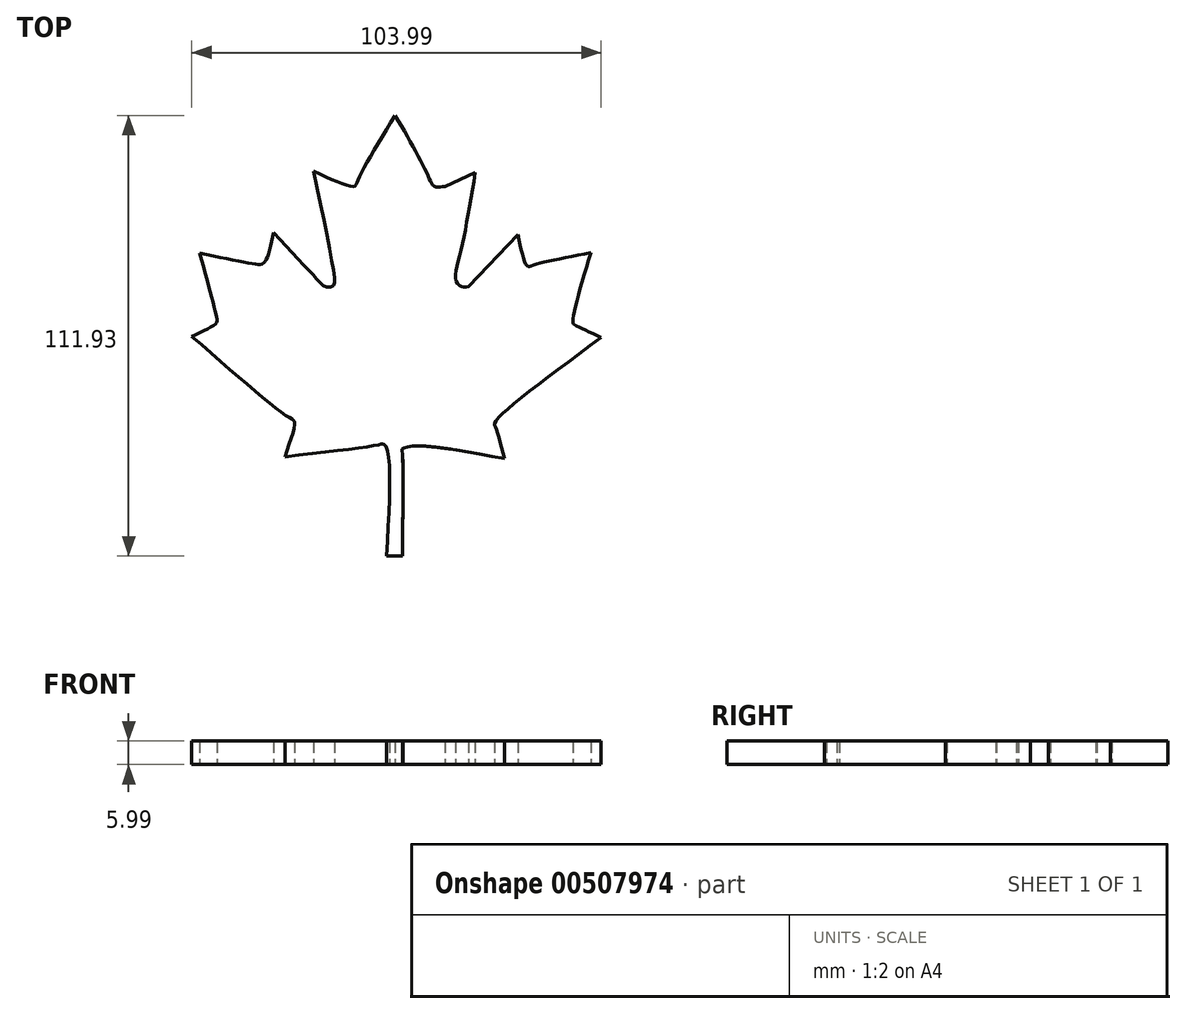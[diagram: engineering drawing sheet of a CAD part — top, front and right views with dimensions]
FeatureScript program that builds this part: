
annotation { "Feature Type Name" : "Feature", "Feature Type Description" : "" }
export const myFeature = defineFeature(function(context is Context, id is Id, definition is map)
    precondition{}
    {
        {
            var Q0;
            Q0=qCreatedBy(makeId("Top.planeOp"),FACE);
            var sketch = newSketch(context, id + "F0", { "sketchPlane" : qUnion([Q0])});
            skFitSpline(sketch, "E0", {"points": [v(-10.33, 22.5) * mm, v(-7.72, 9.18) * mm, v(-7.86, 7.95) * mm, v(-8.82, 7.81) * mm, v(-9.71, 8.57) * mm, v(-11.67, 10.63) * mm, v(-15.43, 14.71) * mm], "startDerivative": vector(10.22, -49.33) * mm, "endDerivative": vector(-18.4, 20.28) * mm});
            skFitSpline(sketch, "E1", {"points": [v(-15.43, 14.71) * mm, v(-16.3, 11.38) * mm, v(-16.88, 10.73) * mm, v(-17.99, 10.73) * mm, v(-24.8, 12.1) * mm], "startDerivative": vector(-2.85, -13.74) * mm, "endDerivative": vector(-20.16, 4.28) * mm});
            skFitSpline(sketch, "E2", {"points": [v(-24.8, 12.1) * mm, v(-22.67, 4.08) * mm, v(-22.71, 3.2) * mm, v(-25.82, 1.52) * mm], "startDerivative": vector(5.31, -19.9) * mm, "endDerivative": vector(-12.37, -5.46) * mm});
            skFitSpline(sketch, "E3", {"points": [v(-25.82, 1.52) * mm, v(-13.38, -8.83) * mm, v(-12.76, -9.35) * mm, v(-14, -13.79) * mm], "startDerivative": vector(28.34, -24.7) * mm, "endDerivative": vector(-6.72, -18.84) * mm});
            skFitSpline(sketch, "E4", {"points": [v(-14, -13.79) * mm, v(-2.03, -12.24) * mm, v(-1.62, -12.13) * mm, v(-1.1, -12.55) * mm, v(-1.08, -26.38) * mm], "startDerivative": vector(40.3, 4.6) * mm, "endDerivative": vector(-2.45, -43.24) * mm});
            skFitSpline(sketch, "E5", {"points": [v(-1.08, -26.38) * mm, v(0.92, -26.38) * mm], "startDerivative": vector(2, 0) * mm, "endDerivative": vector(2, 0) * mm});
            skFitSpline(sketch, "E6", {"points": [v(0.92, -26.38) * mm, v(0.92, -13.22) * mm, v(0.92, -12.82) * mm, v(2.32, -12.42) * mm, v(13.9, -14.02) * mm], "startDerivative": vector(0.6, 43.58) * mm, "endDerivative": vector(36.42, -6.8) * mm});
            skFitSpline(sketch, "E7", {"points": [v(13.9, -14.02) * mm, v(12.8, -10.12) * mm, v(12.7, -9.43) * mm, v(26.18, 1.36) * mm], "startDerivative": vector(-4.19, 16.7) * mm, "endDerivative": vector(32.46, 23.86) * mm});
            skFitSpline(sketch, "E8", {"points": [v(26.18, 1.36) * mm, v(22.88, 2.95) * mm, v(22.58, 3.35) * mm, v(24.88, 12.14) * mm], "startDerivative": vector(-12.17, 5.73) * mm, "endDerivative": vector(6.63, 21.94) * mm});
            skFitSpline(sketch, "E9", {"points": [v(24.88, 12.14) * mm, v(17.5, 10.54) * mm, v(16.8, 10.44) * mm, v(15.6, 14.43) * mm], "startDerivative": vector(-19.12, -3.62) * mm, "endDerivative": vector(-3.25, 15.11) * mm});
            skFitSpline(sketch, "E10", {"points": [v(15.6, 14.43) * mm, v(9.3, 7.84) * mm], "startDerivative": vector(-6.29, -6.59) * mm, "endDerivative": vector(-6.29, -6.59) * mm});
            skFitSpline(sketch, "E11", {"points": [v(9.3, 7.84) * mm, v(8.4, 7.84) * mm, v(7.7, 8.74) * mm, v(8.3, 12.14) * mm, v(10.18, 22.3) * mm], "startDerivative": vector(-6.92, -1.23) * mm, "endDerivative": vector(4.1, 24.96) * mm});
            skFitSpline(sketch, "E12", {"points": [v(10.18, 22.3) * mm, v(6.32, 20.57) * mm], "startDerivative": vector(-3.86, -1.72) * mm, "endDerivative": vector(-3.86, -1.72) * mm});
            skFitSpline(sketch, "E13", {"points": [v(6.32, 20.57) * mm, v(5, 20.57) * mm, v(4.02, 22.3) * mm, v(0, 29.58) * mm], "startDerivative": vector(-6.95, -1.29) * mm, "endDerivative": vector(-9.15, 15.6) * mm});
            skFitSpline(sketch, "E14", {"points": [v(0, 29.58) * mm, v(-4.73, 21.32) * mm, v(-5.22, 20.57) * mm, v(-10.33, 22.5) * mm], "startDerivative": vector(-12.85, -21.18) * mm, "endDerivative": vector(-18.02, 8.47) * mm});
            skSolve(sketch);
        }
        {
            var Q0;
            Q0=makeQuery(id+"F0.imprint","IMPRINT",FACE,{"disambiguationData":[TD([[makeQuery(id+"F0.imprint","IMPRINT",EDGE,{"derivedFrom":sQuery(id+"F0.wireOp",EDGE,"E0")}),1.0]])]});
            extrude(context, id + "F1", {"entities" : qUnion([Q0]), "depth" : 3 * mm});
        }
        {
            var Q0;
            Q0=makeQuery(id+"F1.opExtrude","SWEPT_BODY",BODY,{"disambiguationData":[OSD([sQuery(id+"F0.wireOp",EDGE,"E0"),sQuery(id+"F0.wireOp",EDGE,"E1"),sQuery(id+"F0.wireOp",EDGE,"E2"),sQuery(id+"F0.wireOp",EDGE,"E3"),sQuery(id+"F0.wireOp",EDGE,"E4"),sQuery(id+"F0.wireOp",EDGE,"E5"),sQuery(id+"F0.wireOp",EDGE,"E6"),sQuery(id+"F0.wireOp",EDGE,"E7"),sQuery(id+"F0.wireOp",EDGE,"E8"),sQuery(id+"F0.wireOp",EDGE,"E9"),sQuery(id+"F0.wireOp",EDGE,"E10"),sQuery(id+"F0.wireOp",EDGE,"E11"),sQuery(id+"F0.wireOp",EDGE,"E12"),sQuery(id+"F0.wireOp",EDGE,"E13"),sQuery(id+"F0.wireOp",EDGE,"E14")])]});
            var Q1;
            Q1=qCreatedBy(makeId("Origin.pointOp"),VERTEX);
            transform(context, id + "F2", {"entities" : qUnion([Q0]), "transformType" : TransformType.SCALE_UNIFORMLY, "scale" : 2, "scalePoint" : qUnion([Q1]), "makeCopy" : false});
        }
    });
